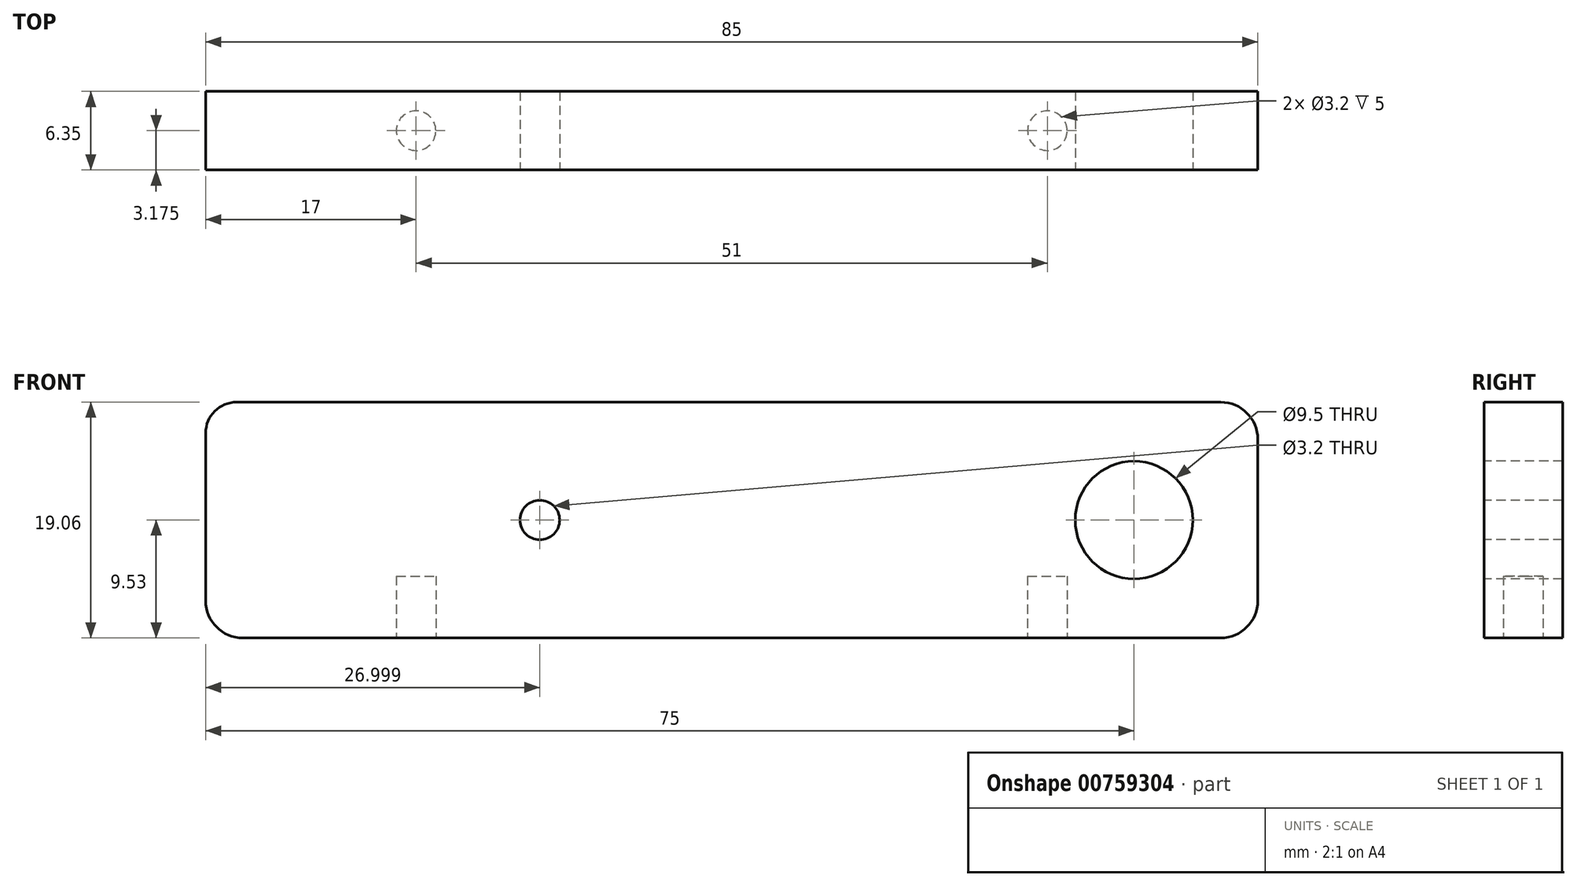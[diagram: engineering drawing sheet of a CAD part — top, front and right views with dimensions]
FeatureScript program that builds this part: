
annotation { "Feature Type Name" : "Feature", "Feature Type Description" : "" }
export const myFeature = defineFeature(function(context is Context, id is Id, definition is map)
    precondition{}
    {
        {
            var Q0;
            Q0=qCreatedBy(makeId("Front.planeOp"),FACE);
            var sketch = newSketch(context, id + "F0", { "sketchPlane" : qUnion([Q0])});
            skLineSegment(sketch, "E0.bottom", {"start": v(-42.5, 9.53) * mm, "end": v(42.5, 9.53) * mm});
            skLineSegment(sketch, "E0.top", {"start": v(-42.5, -9.53) * mm, "end": v(42.5, -9.53) * mm});
            skLineSegment(sketch, "E0.left", {"start": v(-42.5, 9.53) * mm, "end": v(-42.5, -9.53) * mm});
            skLineSegment(sketch, "E0.right", {"start": v(42.5, 9.53) * mm, "end": v(42.5, -9.53) * mm});
            skPoint(sketch, "E0.middle", {"position": v(0, 0) * mm});
            skSolve(sketch);
        }
        {
            var Q0;
            Q0=makeQuery(id+"F0.imprint","IMPRINT",FACE,{"disambiguationData":[TD([[makeQuery(id+"F0.imprint","IMPRINT",EDGE,{"derivedFrom":sQuery(id+"F0.wireOp",EDGE,"E0.bottom")}),-1.0]])]});
            extrude(context, id + "F1", {"entities" : qUnion([Q0]), "depth" : 6.35 * mm, "offsetDistance" : 25 * mm});
        }
        {
            var Q0;
            Q0=makeQuery(id+"F1.opExtrude","SWEPT_FACE",FACE,{"disambiguationData":[OSD([sQuery(id+"F0.wireOp",EDGE,"E0.top")])]});
            var sketch = newSketch(context, id + "F2", { "sketchPlane" : qUnion([Q0])});
            skCircle(sketch, "E1", {"center": v(-25.5, 3.17) * mm, "radius": 1.6 * mm});
            skCircle(sketch, "E2", {"center": v(25.5, 3.17) * mm, "radius": 1.6 * mm});
            skPoint(sketch, "E3.orphan", {"position": v(-42.5, 3.17) * mm});
            skPoint(sketch, "E4.orphan", {"position": v(42.5, 3.17) * mm});
            skSolve(sketch);
        }
        {
            var Q0;
            Q0=makeQuery(id+"F2.imprint","IMPRINT",FACE,{"disambiguationData":[TD([[makeQuery(id+"F2.imprint","IMPRINT",EDGE,{"derivedFrom":sQuery(id+"F2.wireOp",EDGE,"E2")}),1.0]])]});
            var Q1;
            Q1=makeQuery(id+"F2.imprint","IMPRINT",FACE,{"disambiguationData":[TD([[makeQuery(id+"F2.imprint","IMPRINT",EDGE,{"derivedFrom":sQuery(id+"F2.wireOp",EDGE,"E1")}),1.0]])]});
            extrude(context, id + "F3", {"entities" : qUnion([Q0, Q1]), "operationType" : NewBodyOperationType.REMOVE, "oppositeDirection" : true, "depth" : 5 * mm, "offsetDistance" : 25 * mm});
        }
        {
            var Q0;
            Q0=makeQuery(id+"F1.opExtrude","SWEPT_EDGE",EDGE,{"disambiguationData":[OSD([sQuery(id+"F0.wireOp",EDGE,"E0.bottom"),sQuery(id+"F0.wireOp",EDGE,"E0.left")])]});
            fillet(context, id + "F4", {"entities" : qUnion([Q0]), "radius" : 2.5 * mm, "tangentPropagation" : true, "allowEdgeOverflow" : false});
        }
        {
            var Q0;
            Q0=makeQuery(id+"F1.opExtrude","SWEPT_EDGE",EDGE,{"disambiguationData":[OSD([sQuery(id+"F0.wireOp",EDGE,"E0.bottom"),sQuery(id+"F0.wireOp",EDGE,"E0.right")])]});
            fillet(context, id + "F5", {"entities" : qUnion([Q0]), "radius" : 3 * mm, "tangentPropagation" : true, "allowEdgeOverflow" : false});
        }
        {
            var Q0;
            Q0=makeQuery(id+"F1.opExtrude","SWEPT_EDGE",EDGE,{"disambiguationData":[OSD([sQuery(id+"F0.wireOp",EDGE,"E0.top"),sQuery(id+"F0.wireOp",EDGE,"E0.right")])]});
            fillet(context, id + "F6", {"entities" : qUnion([Q0]), "radius" : 3 * mm, "tangentPropagation" : true, "allowEdgeOverflow" : false});
        }
        {
            var Q0;
            Q0=makeQuery(id+"F1.opExtrude","SWEPT_EDGE",EDGE,{"disambiguationData":[OSD([sQuery(id+"F0.wireOp",EDGE,"E0.top"),sQuery(id+"F0.wireOp",EDGE,"E0.left")])]});
            fillet(context, id + "F7", {"entities" : qUnion([Q0]), "radius" : 3 * mm, "tangentPropagation" : true, "allowEdgeOverflow" : false});
        }
        {
            var Q0;
            Q0=makeQuery(id+"F1.opExtrude","CAP_FACE",FACE,{"disambiguationData":[OSD([sQuery(id+"F0.wireOp",EDGE,"E0.bottom"),sQuery(id+"F0.wireOp",EDGE,"E0.top"),sQuery(id+"F0.wireOp",EDGE,"E0.left"),sQuery(id+"F0.wireOp",EDGE,"E0.right")])],"isStart":false});
            var sketch = newSketch(context, id + "F8", { "sketchPlane" : qUnion([Q0])});
            skCircle(sketch, "E5", {"center": v(32.5, 0) * mm, "radius": 4.75 * mm});
            skPoint(sketch, "E6.orphan", {"position": v(42.5, 0) * mm});
            skSolve(sketch);
        }
        {
            var Q0;
            Q0=makeQuery(id+"F8.imprint","IMPRINT",FACE,{"disambiguationData":[TD([[makeQuery(id+"F8.imprint","IMPRINT",EDGE,{"derivedFrom":sQuery(id+"F8.wireOp",EDGE,"E5")}),1.0]])]});
            extrude(context, id + "F9", {"entities" : qUnion([Q0]), "operationType" : NewBodyOperationType.REMOVE, "oppositeDirection" : true, "depth" : 25 * mm, "offsetDistance" : 25 * mm});
        }
        {
            var Q0;
            Q0=makeQuery(id+"F1.opExtrude","CAP_FACE",FACE,{"disambiguationData":[OSD([sQuery(id+"F0.wireOp",EDGE,"E0.bottom"),sQuery(id+"F0.wireOp",EDGE,"E0.top"),sQuery(id+"F0.wireOp",EDGE,"E0.left"),sQuery(id+"F0.wireOp",EDGE,"E0.right")])],"isStart":false});
            var sketch = newSketch(context, id + "F10", { "sketchPlane" : qUnion([Q0])});
            skCircle(sketch, "E7", {"center": v(-15.5, 0) * mm, "radius": 1.6 * mm});
            skPoint(sketch, "E8.orphan", {"position": v(-42.5, 0.25) * mm});
            skSolve(sketch);
        }
        {
            var Q0;
            Q0=makeQuery(id+"F10.imprint","IMPRINT",FACE,{"disambiguationData":[TD([[makeQuery(id+"F10.imprint","IMPRINT",EDGE,{"derivedFrom":sQuery(id+"F10.wireOp",EDGE,"E7")}),1.0]])]});
            extrude(context, id + "F11", {"entities" : qUnion([Q0]), "operationType" : NewBodyOperationType.REMOVE, "oppositeDirection" : true, "depth" : 25 * mm, "offsetDistance" : 25 * mm});
        }
    });
